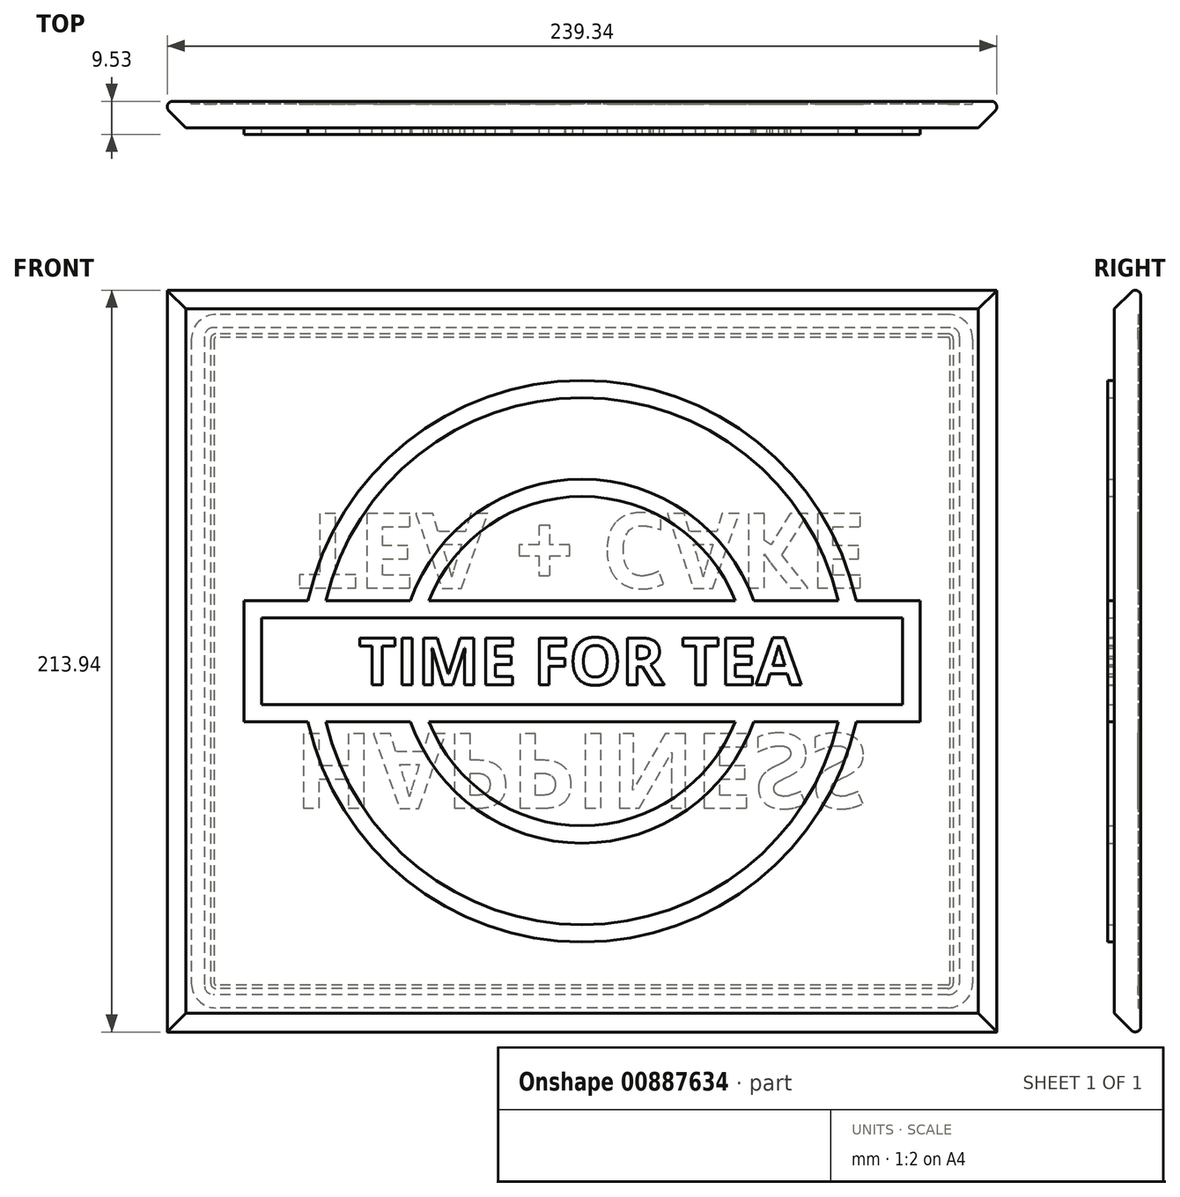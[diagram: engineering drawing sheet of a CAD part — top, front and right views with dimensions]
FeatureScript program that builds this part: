
annotation { "Feature Type Name" : "Feature", "Feature Type Description" : "" }
export const myFeature = defineFeature(function(context is Context, id is Id, definition is map)
    precondition{}
    {
        {
            var Q0;
            Q0=qCreatedBy(makeId("Front.planeOp"),FACE);
            var sketch = newSketch(context, id + "F0", { "sketchPlane" : qUnion([Q0])});
            skArc(sketch, "E0", {"start": v(79.09, 17.5) * mm, "mid": v(0, 81) * mm, "end": v(-79.09, 17.5) * mm});
            skLineSegment(sketch, "E1.bottom", {"start": v(-97.5, -17.5) * mm, "end": v(-79.09, -17.5) * mm});
            skLineSegment(sketch, "E1.top", {"start": v(-97.5, 17.5) * mm, "end": v(-79.09, 17.5) * mm});
            skLineSegment(sketch, "E1.left", {"start": v(-97.5, -17.5) * mm, "end": v(-97.5, 17.5) * mm});
            skLineSegment(sketch, "E1.right", {"start": v(97.5, -17.5) * mm, "end": v(97.5, 17.5) * mm});
            skArc(sketch, "E2.trimOffspring", {"start": v(-79.09, -17.5) * mm, "mid": v(0, -81) * mm, "end": v(79.09, -17.5) * mm});
            skArc(sketch, "E3.0", {"start": v(73.96, 17.5) * mm, "mid": v(0, 76) * mm, "end": v(-73.96, 17.5) * mm});
            skArc(sketch, "E4.0", {"start": v(-73.96, -17.5) * mm, "mid": v(0, -76) * mm, "end": v(73.96, -17.5) * mm});
            skLineSegment(sketch, "E5.0", {"start": v(-92.5, 12.5) * mm, "end": v(92.5, 12.5) * mm});
            skLineSegment(sketch, "E5.1", {"start": v(-92.5, -12.5) * mm, "end": v(-92.5, 12.5) * mm});
            skLineSegment(sketch, "E5.2", {"start": v(-92.5, -12.5) * mm, "end": v(92.5, -12.5) * mm});
            skArc(sketch, "E6", {"start": v(44.16, 17.5) * mm, "mid": v(0, 47.5) * mm, "end": v(-44.16, 17.5) * mm});
            skArc(sketch, "E7.trimOffspring", {"start": v(-44.16, -17.5) * mm, "mid": v(0, -47.5) * mm, "end": v(44.16, -17.5) * mm});
            skLineSegment(sketch, "E8.0", {"start": v(92.5, -12.5) * mm, "end": v(92.5, 12.5) * mm});
            skArc(sketch, "E9", {"start": v(49.5, 17.5) * mm, "mid": v(0, 52.5) * mm, "end": v(-49.5, 17.5) * mm});
            skArc(sketch, "E10.trimOffspring", {"start": v(-49.5, -17.5) * mm, "mid": v(0, -52.5) * mm, "end": v(49.5, -17.5) * mm});
            skLineSegment(sketch, "E11.trimOffspring", {"start": v(-73.96, 17.5) * mm, "end": v(-49.5, 17.5) * mm});
            skLineSegment(sketch, "E12.trimOffspring", {"start": v(-44.16, 17.5) * mm, "end": v(44.16, 17.5) * mm});
            skLineSegment(sketch, "E13.trimOffspring", {"start": v(49.5, 17.5) * mm, "end": v(73.96, 17.5) * mm});
            skLineSegment(sketch, "E14.trimOffspring", {"start": v(79.09, 17.5) * mm, "end": v(97.5, 17.5) * mm});
            skLineSegment(sketch, "E15.trimOffspring", {"start": v(79.09, -17.5) * mm, "end": v(97.5, -17.5) * mm});
            skLineSegment(sketch, "E16.trimOffspring", {"start": v(49.5, -17.5) * mm, "end": v(73.96, -17.5) * mm});
            skLineSegment(sketch, "E17.trimOffspring", {"start": v(-44.16, -17.5) * mm, "end": v(44.16, -17.5) * mm});
            skLineSegment(sketch, "E18.trimOffspring", {"start": v(-73.96, -17.5) * mm, "end": v(-49.5, -17.5) * mm});
            skSolve(sketch);
        }
        {
            var Q0;
            Q0 = qSketchRegion(id + "F0", true);
            extrude(context, id + "F1", {"entities" : qUnion([Q0]), "depth" : 1.9 * mm, "offsetDistance" : 25.4 * mm});
        }
        {
            var Q0;
            Q0=makeQuery(id+"F0.imprint","IMPRINT",FACE,{"disambiguationData":[TD([[makeQuery(id+"F0.imprint","IMPRINT",EDGE,{"derivedFrom":sQuery(id+"F0.wireOp",EDGE,"E0")}),1.0]])]});
            var sketch = newSketch(context, id + "F2", { "sketchPlane" : qUnion([Q0])});
            skLineSegment(sketch, "E19.bottom", {"start": v(123.83, 111.12) * mm, "end": v(-123.83, 111.12) * mm});
            skLineSegment(sketch, "E19.top", {"start": v(123.83, -111.13) * mm, "end": v(-123.83, -111.13) * mm});
            skLineSegment(sketch, "E19.left", {"start": v(123.83, 111.13) * mm, "end": v(123.83, -111.12) * mm});
            skLineSegment(sketch, "E19.right", {"start": v(-123.83, 111.12) * mm, "end": v(-123.83, -111.13) * mm});
            skPoint(sketch, "E19.middle", {"position": v(0, 0) * mm});
            skSolve(sketch);
        }
        {
            var Q0;
            Q0 = qSketchRegion(id + "F2", true);
            extrude(context, id + "F3", {"entities" : qUnion([Q0]), "operationType" : NewBodyOperationType.ADD, "oppositeDirection" : true, "depth" : 7.62 * mm, "offsetDistance" : 25.4 * mm});
        }
        {
            var Q0;
            Q0=makeQuery(id+"F0.imprint","IMPRINT",FACE,{"disambiguationData":[TD([[makeQuery(id+"F0.imprint","IMPRINT",EDGE,{"derivedFrom":sQuery(id+"F0.wireOp",EDGE,"E5.0")}),-1.0]])]});
            var sketch = newSketch(context, id + "F4", { "sketchPlane" : qUnion([Q0])});
            skText(sketch, "E20", { "text": "TIME FOR TEA", "fontName": "OpenSans-Bold.ttf"});
            const initialGuessF4  = {"E20": [-0.06456, -0.0068, 1, 0, 0.0136]};
            skSetInitialGuess(sketch, initialGuessF4);
            skSolve(sketch);
        }
        {
            var Q0;
            Q0 = qSketchRegion(id + "F4", true);
            extrude(context, id + "F5", {"entities" : qUnion([Q0]), "operationType" : NewBodyOperationType.ADD, "depth" : 1.9 * mm, "offsetDistance" : 25.4 * mm});
        }
        {
            var Q0;
            Q0=makeQuery(id+"F3.opExtrude","CAP_EDGE",EDGE,{"disambiguationData":[OSD([sQuery(id+"F2.wireOp",EDGE,"E19.left")])],"isStart":true});
            var Q1;
            Q1=makeQuery(id+"F3.opExtrude","CAP_EDGE",EDGE,{"disambiguationData":[OSD([sQuery(id+"F2.wireOp",EDGE,"E19.bottom")])],"isStart":true});
            var Q2;
            Q2=makeQuery(id+"F3.opExtrude","CAP_EDGE",EDGE,{"disambiguationData":[OSD([sQuery(id+"F2.wireOp",EDGE,"E19.right")])],"isStart":true});
            var Q3;
            Q3=makeQuery(id+"F3.opExtrude","CAP_EDGE",EDGE,{"disambiguationData":[OSD([sQuery(id+"F2.wireOp",EDGE,"E19.top")])],"isStart":true});
            chamfer(context, id + "F6", {"entities" : qUnion([Q0, Q1, Q2, Q3]), "width" : 9.52 * mm, "tangentPropagation" : true});
        }
        {
            var Q0;
            Q0=makeQuery(id+"F3.opExtrude","CAP_FACE",FACE,{"disambiguationData":[OSD([sQuery(id+"F2.wireOp",EDGE,"E19.bottom"),sQuery(id+"F2.wireOp",EDGE,"E19.top"),sQuery(id+"F2.wireOp",EDGE,"E19.left"),sQuery(id+"F2.wireOp",EDGE,"E19.right")])],"isStart":false});
            fillet(context, id + "F7", {"entities" : qUnion([Q0]), "radius" : 1.59 * mm, "tangentPropagation" : true, "allowEdgeOverflow" : false});
        }
        {
            var Q0;
            Q0=makeQuery(id+"F3.opExtrude","CAP_FACE",FACE,{"disambiguationData":[OSD([sQuery(id+"F2.wireOp",EDGE,"E19.bottom"),sQuery(id+"F2.wireOp",EDGE,"E19.top"),sQuery(id+"F2.wireOp",EDGE,"E19.left"),sQuery(id+"F2.wireOp",EDGE,"E19.right")])],"isStart":false});
            var sketch = newSketch(context, id + "F8", { "sketchPlane" : qUnion([Q0])});
            skPoint(sketch, "E21", {"position": v(0, -31.75) * mm});
            skPoint(sketch, "E22", {"position": v(0, 31.75) * mm});
            skText(sketch, "E23", { "text": "HAPPINESS", "fontName": "OpenSans-Bold.ttf"});
            skText(sketch, "E24", { "text": "TEA + CAKE", "fontName": "OpenSans-Bold.ttf"});
            const initialGuessF8  = {"E23": [0.0831, -0.02096, -1, 0, 0.02159], "E24": [0.08211, 0.04254, -1, 0, 0.0216]};
            skSetInitialGuess(sketch, initialGuessF8);
            skSolve(sketch);
        }
        {
            var Q0;
            Q0 = qSketchRegion(id + "F8", true);
            extrude(context, id + "F9", {"entities" : qUnion([Q0]), "operationType" : NewBodyOperationType.REMOVE, "oppositeDirection" : true, "depth" : 0.76 * mm, "offsetDistance" : 25.4 * mm});
        }
        {
            var Q0;
            {var subQ0=sQuery(id+"F2.wireOp",EDGE,"E19.right");var subQ1=sQuery(id+"F2.wireOp",EDGE,"E19.left");var subQ2=sQuery(id+"F2.wireOp",EDGE,"E19.top");var subQ3=sQuery(id+"F2.wireOp",EDGE,"E19.bottom");var subQ4=makeQuery(id+"F3.opExtrude","CAP_FACE",FACE,{"disambiguationData":[OSD([subQ3,subQ2,subQ1,subQ0])],"isStart":false});Q0=makeQuery(id+"F9.boolean.opBoolean","SPLIT",FACE,{"disambiguationData":[TD([makeQuery(id+"F9.opExtrude","SWEPT_FACE",FACE,{"disambiguationData":[OSD([sQuery(id+"F8.wireOp",EDGE,"E23.sketch_text.stroke-0")])]})])],"derivedFrom":subQ4});}
            var sketch = newSketch(context, id + "F10", { "sketchPlane" : qUnion([Q0])});
            skLineSegment(sketch, "E25.bottom", {"start": v(-105.6, 100.01) * mm, "end": v(105.6, 100.01) * mm});
            skLineSegment(sketch, "E25.top", {"start": v(-105.6, -100.01) * mm, "end": v(105.6, -100.01) * mm});
            skLineSegment(sketch, "E25.left", {"start": v(-112.71, 92.9) * mm, "end": v(-112.71, -92.9) * mm});
            skLineSegment(sketch, "E25.right", {"start": v(112.71, 92.9) * mm, "end": v(112.71, -92.9) * mm});
            skPoint(sketch, "E25.middle", {"position": v(0, 0) * mm});
            skLineSegment(sketch, "E26.bottom", {"start": v(-106.36, 96.2) * mm, "end": v(106.36, 96.2) * mm});
            skLineSegment(sketch, "E26.top", {"start": v(-105.6, -96.2) * mm, "end": v(106.36, -96.2) * mm});
            skLineSegment(sketch, "E26.left", {"start": v(-108.9, 93.66) * mm, "end": v(-108.9, -92.9) * mm});
            skLineSegment(sketch, "E26.right", {"start": v(108.9, 93.66) * mm, "end": v(108.9, -93.66) * mm});
            skLineSegment(sketch, "E27.bottom", {"start": v(-105.6, 94.42) * mm, "end": v(105.6, 94.42) * mm});
            skLineSegment(sketch, "E27.top", {"start": v(-105.6, -94.42) * mm, "end": v(105.6, -94.42) * mm});
            skLineSegment(sketch, "E27.left", {"start": v(-107.12, 92.9) * mm, "end": v(-107.12, -92.9) * mm});
            skLineSegment(sketch, "E27.right", {"start": v(107.12, 92.9) * mm, "end": v(107.12, -92.9) * mm});
            skLineSegment(sketch, "E28.bottom", {"start": v(-105.6, 93.4) * mm, "end": v(105.6, 93.4) * mm});
            skLineSegment(sketch, "E28.top", {"start": v(-105.6, -93.4) * mm, "end": v(105.6, -93.4) * mm});
            skLineSegment(sketch, "E28.left", {"start": v(-106.1, 92.9) * mm, "end": v(-106.1, -92.9) * mm});
            skLineSegment(sketch, "E28.right", {"start": v(106.1, 92.9) * mm, "end": v(106.1, -92.9) * mm});
            skPoint(sketch, "E29.visualSharp", {"position": v(-112.71, -100.01) * mm});
            skArc(sketch, "E29.filletArc", {"start": v(-112.71, -92.9) * mm, "mid": v(-110.63, -97.93) * mm, "end": v(-105.6, -100.01) * mm});
            skPoint(sketch, "E30.visualSharp", {"position": v(-112.71, 100.01) * mm});
            skArc(sketch, "E30.filletArc", {"start": v(-105.6, 100.01) * mm, "mid": v(-110.63, 97.93) * mm, "end": v(-112.71, 92.9) * mm});
            skPoint(sketch, "E31.visualSharp", {"position": v(112.71, 100.01) * mm});
            skArc(sketch, "E31.filletArc", {"start": v(112.71, 92.9) * mm, "mid": v(110.63, 97.93) * mm, "end": v(105.6, 100.01) * mm});
            skPoint(sketch, "E32.visualSharp", {"position": v(112.71, -100.01) * mm});
            skArc(sketch, "E32.filletArc", {"start": v(105.6, -100.01) * mm, "mid": v(110.63, -97.93) * mm, "end": v(112.71, -92.9) * mm});
            skPoint(sketch, "E33.visualSharp", {"position": v(108.9, -96.2) * mm});
            skArc(sketch, "E33.filletArc", {"start": v(106.36, -96.2) * mm, "mid": v(108.16, -95.46) * mm, "end": v(108.9, -93.66) * mm});
            skPoint(sketch, "E34.visualSharp", {"position": v(108.9, 96.2) * mm});
            skArc(sketch, "E34.filletArc", {"start": v(108.9, 93.66) * mm, "mid": v(108.16, 95.46) * mm, "end": v(106.36, 96.2) * mm});
            skPoint(sketch, "E35.visualSharp", {"position": v(-108.9, 96.2) * mm});
            skArc(sketch, "E35.filletArc", {"start": v(-106.36, 96.2) * mm, "mid": v(-108.16, 95.46) * mm, "end": v(-108.9, 93.66) * mm});
            skPoint(sketch, "E36.visualSharp", {"position": v(-108.9, -96.2) * mm});
            skArc(sketch, "E36.filletArc", {"start": v(-108.9, -92.9) * mm, "mid": v(-107.94, -95.24) * mm, "end": v(-105.6, -96.2) * mm});
            skPoint(sketch, "E37.visualSharp", {"position": v(106.1, -93.4) * mm});
            skArc(sketch, "E37.filletArc", {"start": v(105.6, -93.4) * mm, "mid": v(105.96, -93.26) * mm, "end": v(106.1, -92.9) * mm});
            skPoint(sketch, "E38.visualSharp", {"position": v(-106.1, -93.4) * mm});
            skArc(sketch, "E38.filletArc", {"start": v(-106.1, -92.9) * mm, "mid": v(-105.96, -93.26) * mm, "end": v(-105.6, -93.4) * mm});
            skPoint(sketch, "E39.visualSharp", {"position": v(-106.1, 93.4) * mm});
            skArc(sketch, "E39.filletArc", {"start": v(-105.6, 93.4) * mm, "mid": v(-105.96, 93.26) * mm, "end": v(-106.1, 92.9) * mm});
            skPoint(sketch, "E40.visualSharp", {"position": v(106.1, 93.4) * mm});
            skArc(sketch, "E40.filletArc", {"start": v(106.1, 92.9) * mm, "mid": v(105.96, 93.26) * mm, "end": v(105.6, 93.4) * mm});
            skPoint(sketch, "E41.visualSharp", {"position": v(107.12, -94.42) * mm});
            skArc(sketch, "E41.filletArc", {"start": v(105.6, -94.42) * mm, "mid": v(106.68, -93.98) * mm, "end": v(107.12, -92.9) * mm});
            skPoint(sketch, "E42.visualSharp", {"position": v(-107.12, -94.42) * mm});
            skArc(sketch, "E42.filletArc", {"start": v(-107.12, -92.9) * mm, "mid": v(-106.68, -93.98) * mm, "end": v(-105.6, -94.42) * mm});
            skPoint(sketch, "E43.visualSharp", {"position": v(-107.12, 94.42) * mm});
            skArc(sketch, "E43.filletArc", {"start": v(-105.6, 94.42) * mm, "mid": v(-106.68, 93.98) * mm, "end": v(-107.12, 92.9) * mm});
            skPoint(sketch, "E44.visualSharp", {"position": v(107.12, 94.42) * mm});
            skArc(sketch, "E44.filletArc", {"start": v(107.12, 92.9) * mm, "mid": v(106.68, 93.98) * mm, "end": v(105.6, 94.42) * mm});
            skSolve(sketch);
        }
        {
            var Q0;
            Q0=makeQuery(id+"F10.imprint","IMPRINT",FACE,{"disambiguationData":[TD([[makeQuery(id+"F10.imprint","IMPRINT",EDGE,{"derivedFrom":sQuery(id+"F10.wireOp",EDGE,"E25.bottom")}),-1.0]])]});
            var Q1;
            Q1=makeQuery(id+"F10.imprint","IMPRINT",FACE,{"disambiguationData":[TD([[makeQuery(id+"F10.imprint","IMPRINT",EDGE,{"derivedFrom":sQuery(id+"F10.wireOp",EDGE,"E27.bottom")}),-1.0]])]});
            extrude(context, id + "F11", {"entities" : qUnion([Q0, Q1]), "operationType" : NewBodyOperationType.REMOVE, "oppositeDirection" : true, "depth" : 0.76 * mm, "offsetDistance" : 25.4 * mm});
        }
    });
